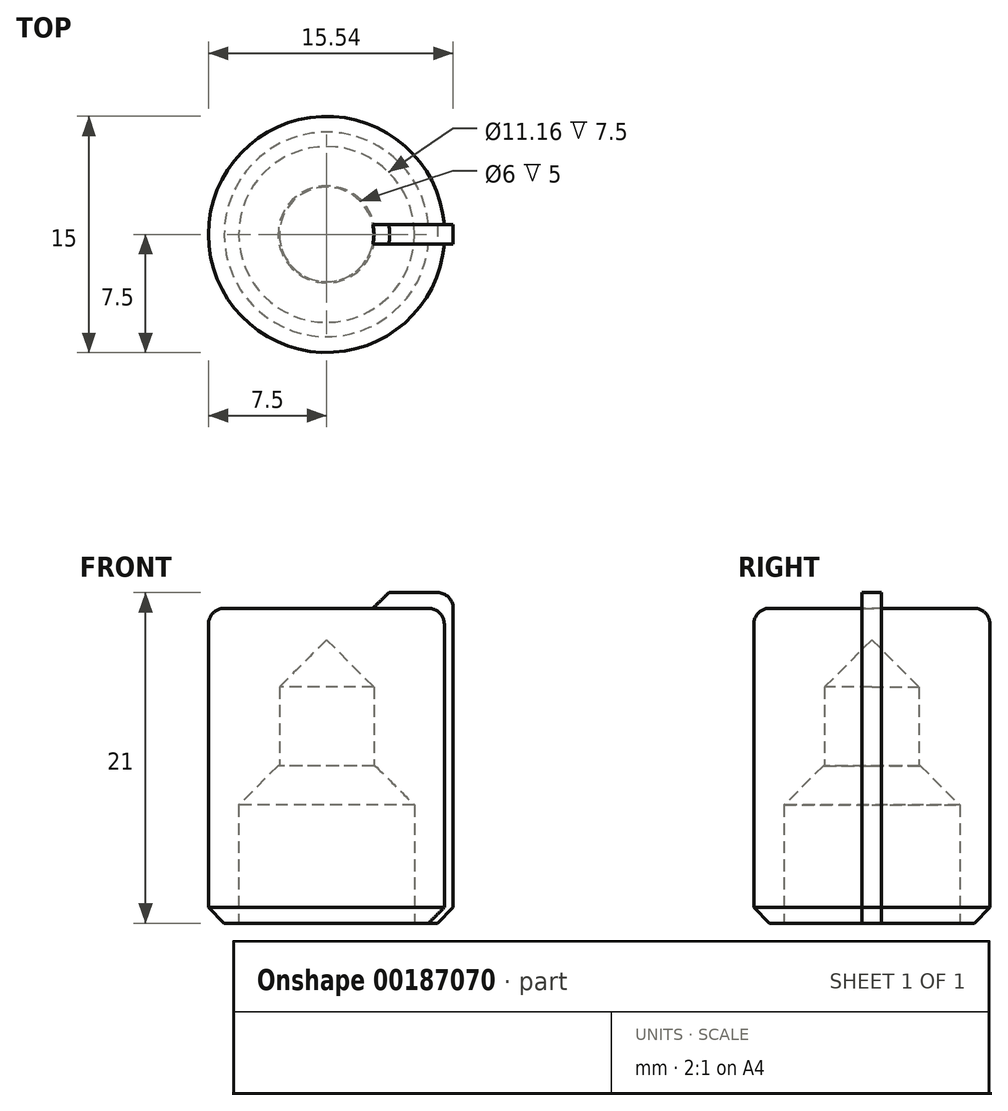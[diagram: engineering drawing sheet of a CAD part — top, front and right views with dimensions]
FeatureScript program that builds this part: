
annotation { "Feature Type Name" : "Feature", "Feature Type Description" : "" }
export const myFeature = defineFeature(function(context is Context, id is Id, definition is map)
    precondition{}
    {
        {
            var Q0;
            Q0=qCreatedBy(makeId("Top.planeOp"),FACE);
            var sketch = newSketch(context, id + "F0", { "sketchPlane" : qUnion([Q0])});
            skCircle(sketch, "E0", {"center": v(0, 0) * mm, "radius": 7.5 * mm});
            skCircle(sketch, "E1", {"center": v(0, 0) * mm, "radius": 3 * mm});
            skLineSegment(sketch, "E2", {"start": v(3, 0) * mm, "end": v(7.5, 0) * mm, "construction": true});
            skLineSegment(sketch, "E3.bottom", {"start": v(8.04, -0.61) * mm, "end": v(2.94, -0.61) * mm});
            skLineSegment(sketch, "E3.top", {"start": v(8.04, 0.61) * mm, "end": v(2.94, 0.61) * mm});
            skLineSegment(sketch, "E3.left", {"start": v(8.04, -0.61) * mm, "end": v(8.04, 0.61) * mm});
            skLineSegment(sketch, "E3.right", {"start": v(2.94, -0.61) * mm, "end": v(2.94, 0.61) * mm});
            skPoint(sketch, "E3.middle", {"position": v(5.49, 0) * mm});
            skPoint(sketch, "E4", {"position": v(5.25, 0) * mm});
            skCircle(sketch, "E5", {"center": v(0, 0) * mm, "radius": 5.58 * mm});
            skSolve(sketch);
        }
        {
            var Q0;
            {var subQ0=sQuery(id+"F0.wireOp",EDGE,"E3.right");Q0=makeQuery(id+"F0.imprint","IMPRINT",FACE,{"disambiguationData":[TD([[makeQuery(id+"F0.imprint","IMPRINT",EDGE,{"derivedFrom":subQ0}),-1.0]])]});}
            var Q1;
            {var subQ0=sQuery(id+"F0.wireOp",EDGE,"E3.bottom");var subQ1=sQuery(id+"F0.wireOp",EDGE,"E0");var subQ2=makeQuery(id+"F0.imprint","INTERSECT",VERTEX,{"derivedFrom":[subQ1,subQ0]});Q1=makeQuery(id+"F0.imprint","IMPRINT",FACE,{"disambiguationData":[TD([[makeQuery(id+"F0.imprint","IMPRINT",EDGE,{"disambiguationData":[TD([[subQ2,1.0]])],"derivedFrom":subQ1}),1.0]])]});}
            var Q2;
            {var subQ1=sQuery(id+"F0.wireOp",EDGE,"E3.bottom");var subQ6=sQuery(id+"F0.wireOp",EDGE,"E5");var subQ7=makeQuery(id+"F0.imprint","INTERSECT",VERTEX,{"derivedFrom":[subQ1,subQ6]});Q2=makeQuery(id+"F0.imprint","IMPRINT",FACE,{"disambiguationData":[TD([[makeQuery(id+"F0.imprint","IMPRINT",EDGE,{"disambiguationData":[TD([[subQ7,1.0]])],"derivedFrom":subQ6}),1.0]])]});}
            var Q3;
            {var subQ0=sQuery(id+"F0.wireOp",EDGE,"E3.right");Q3=makeQuery(id+"F0.imprint","IMPRINT",FACE,{"disambiguationData":[TD([[makeQuery(id+"F0.imprint","IMPRINT",EDGE,{"derivedFrom":subQ0}),1.0]])]});}
            var Q4;
            {var subQ0=sQuery(id+"F0.wireOp",EDGE,"E3.bottom");var subQ1=sQuery(id+"F0.wireOp",EDGE,"E0");var subQ2=makeQuery(id+"F0.imprint","INTERSECT",VERTEX,{"derivedFrom":[subQ1,subQ0]});Q4=makeQuery(id+"F0.imprint","IMPRINT",FACE,{"disambiguationData":[TD([[makeQuery(id+"F0.imprint","IMPRINT",EDGE,{"disambiguationData":[TD([[subQ2,-1.0]])],"derivedFrom":subQ1}),1.0]])]});}
            var Q5;
            {var subQ1=sQuery(id+"F0.wireOp",EDGE,"E3.bottom");var subQ6=sQuery(id+"F0.wireOp",EDGE,"E5");var subQ7=makeQuery(id+"F0.imprint","INTERSECT",VERTEX,{"derivedFrom":[subQ1,subQ6]});Q5=makeQuery(id+"F0.imprint","IMPRINT",FACE,{"disambiguationData":[TD([[makeQuery(id+"F0.imprint","IMPRINT",EDGE,{"disambiguationData":[TD([[subQ7,-1.0]])],"derivedFrom":subQ6}),1.0]])]});}
            extrude(context, id + "F1", {"entities" : qUnion([Q0, Q1, Q2, Q3, Q4, Q5]), "depth" : 20 * mm});
        }
        {
            var Q0;
            {var subQ5=sQuery(id+"F0.wireOp",EDGE,"E3.left");Q0=makeQuery(id+"F0.imprint","IMPRINT",FACE,{"disambiguationData":[TD([[makeQuery(id+"F0.imprint","IMPRINT",EDGE,{"derivedFrom":subQ5}),1.0]])]});}
            var Q1;
            {var subQ0=sQuery(id+"F0.wireOp",EDGE,"E3.bottom");var subQ1=sQuery(id+"F0.wireOp",EDGE,"E0");var subQ2=makeQuery(id+"F0.imprint","INTERSECT",VERTEX,{"derivedFrom":[subQ1,subQ0]});Q1=makeQuery(id+"F0.imprint","IMPRINT",FACE,{"disambiguationData":[TD([[makeQuery(id+"F0.imprint","IMPRINT",EDGE,{"disambiguationData":[TD([[subQ2,-1.0]])],"derivedFrom":subQ1}),1.0]])]});}
            var Q2;
            {var subQ1=sQuery(id+"F0.wireOp",EDGE,"E3.bottom");var subQ6=sQuery(id+"F0.wireOp",EDGE,"E5");var subQ7=makeQuery(id+"F0.imprint","INTERSECT",VERTEX,{"derivedFrom":[subQ1,subQ6]});Q2=makeQuery(id+"F0.imprint","IMPRINT",FACE,{"disambiguationData":[TD([[makeQuery(id+"F0.imprint","IMPRINT",EDGE,{"disambiguationData":[TD([[subQ7,-1.0]])],"derivedFrom":subQ6}),1.0]])]});}
            extrude(context, id + "F2", {"entities" : qUnion([Q0, Q1, Q2]), "operationType" : NewBodyOperationType.ADD, "depth" : 21 * mm});
        }
        {
            var Q0;
            Q0=makeQuery(id+"F0.imprint","IMPRINT",FACE,{"disambiguationData":[TD([[makeQuery(id+"F0.imprint","IMPRINT",EDGE,{"derivedFrom":sQuery(id+"F0.wireOp",EDGE,"E1")}),1.0]])]});
            extrude(context, id + "F3", {"entities" : qUnion([Q0]), "operationType" : NewBodyOperationType.REMOVE, "depth" : 18 * mm});
        }
        {
            var Q0;
            {var subQ1=sQuery(id+"F0.wireOp",EDGE,"E3.bottom");var subQ6=sQuery(id+"F0.wireOp",EDGE,"E5");var subQ7=makeQuery(id+"F0.imprint","INTERSECT",VERTEX,{"derivedFrom":[subQ1,subQ6]});Q0=makeQuery(id+"F0.imprint","IMPRINT",FACE,{"disambiguationData":[TD([[makeQuery(id+"F0.imprint","IMPRINT",EDGE,{"disambiguationData":[TD([[subQ7,1.0]])],"derivedFrom":subQ6}),1.0]])]});}
            var Q1;
            {var subQ1=sQuery(id+"F0.wireOp",EDGE,"E3.bottom");var subQ6=sQuery(id+"F0.wireOp",EDGE,"E5");var subQ7=makeQuery(id+"F0.imprint","INTERSECT",VERTEX,{"derivedFrom":[subQ1,subQ6]});Q1=makeQuery(id+"F0.imprint","IMPRINT",FACE,{"disambiguationData":[TD([[makeQuery(id+"F0.imprint","IMPRINT",EDGE,{"disambiguationData":[TD([[subQ7,-1.0]])],"derivedFrom":subQ6}),1.0]])]});}
            extrude(context, id + "F4", {"entities" : qUnion([Q0, Q1]), "operationType" : NewBodyOperationType.REMOVE, "depth" : 10 * mm});
        }
        {
            var Q0;
            Q0=makeQuery(id+"F1.opExtrude","CAP_EDGE",EDGE,{"disambiguationData":[OSD([sQuery(id+"F0.wireOp",EDGE,"E0")])],"isStart":false});
            var Q1;
            Q1=makeQuery(id+"F2.opExtrude","CAP_EDGE",EDGE,{"disambiguationData":[OSD([sQuery(id+"F0.wireOp",EDGE,"E3.left")])],"isStart":false});
            fillet(context, id + "F10", {"entities" : qUnion([Q0, Q1]), "radius" : 1 * mm, "tangentPropagation" : true, "allowEdgeOverflow" : false});
        }
        {
            var Q0;
            Q0=makeQuery(id+"F3.boolean.opBoolean","COPY",EDGE,{"derivedFrom":makeQuery(id+"F3.opExtrude","CAP_EDGE",EDGE,{"disambiguationData":[OSD([sQuery(id+"F0.wireOp",EDGE,"E1")])],"isStart":false})});
            chamfer(context, id + "F5", {"entities" : qUnion([Q0]), "width" : 3 * mm, "tangentPropagation" : true});
        }
        {
            var Q0;
            Q0=makeQuery(id+"F2.opExtrude","CAP_EDGE",EDGE,{"disambiguationData":[OSD([sQuery(id+"F0.wireOp",EDGE,"E1")])],"isStart":false});
            chamfer(context, id + "F6", {"entities" : qUnion([Q0]), "width" : 1 * mm, "tangentPropagation" : true});
        }
        {
            var Q0;
            Q0=makeQuery(id+"F1.opExtrude","CAP_EDGE",EDGE,{"disambiguationData":[OSD([sQuery(id+"F0.wireOp",EDGE,"E0")])],"isStart":true});
            chamfer(context, id + "F7", {"entities" : qUnion([Q0]), "width" : 1 * mm, "tangentPropagation" : true});
        }
        {
            var Q0;
            Q0=makeQuery(id+"F2.opExtrude","CAP_EDGE",EDGE,{"disambiguationData":[OSD([sQuery(id+"F0.wireOp",EDGE,"E3.left")])],"isStart":true});
            chamfer(context, id + "F8", {"entities" : qUnion([Q0]), "width" : 1 * mm, "tangentPropagation" : true});
        }
        {
            var Q0;
            Q0=makeQuery(id+"F4.boolean.opBoolean","COPY",EDGE,{"derivedFrom":makeQuery(id+"F4.opExtrude","CAP_EDGE",EDGE,{"disambiguationData":[OSD([sQuery(id+"F0.wireOp",EDGE,"E5")])],"isStart":false})});
            chamfer(context, id + "F9", {"entities" : qUnion([Q0]), "width" : 2.5 * mm, "tangentPropagation" : true});
        }
    });
